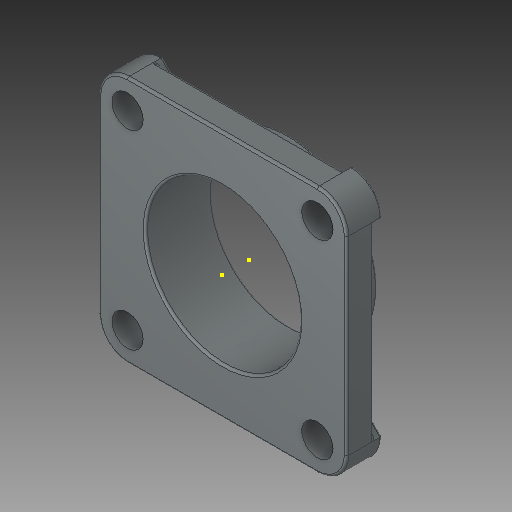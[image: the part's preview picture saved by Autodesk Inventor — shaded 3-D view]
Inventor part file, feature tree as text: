
AUTODESK INVENTOR PART (.ipt)
format: ipt  version: 2019 (Build 230136000, 136)  size: 444,928 bytes
history: native  units: in
note: dims shown in document units (in); Inventor stores cm internally (conversion verified against a paired STEP export)
features: sketch x10, other x3
ambient origin geometry x8: Origin, YZ Plane, XZ Plane, XY Plane, X Axis, Y Axis, Z Axis, Center Point
bodies: Solid1 (feature_tree)
feature tree (13):
  other  "project flange bearing part1.ipt"
  other  "Solid1::project flange bearing part1.ipt"
  other  "TaggingFeature1"
  sketch  "Sketch1"  dims[d0=0.3937in]
  sketch  "Sketch2"
  sketch  "Sketch3"
  sketch  "Sketch4"
  sketch  "Sketch5"
  sketch  "Sketch6"
  sketch  "Sketch7"
  sketch  "Sketch8"
  sketch  "Sketch9"
  sketch  "Sketch10"
